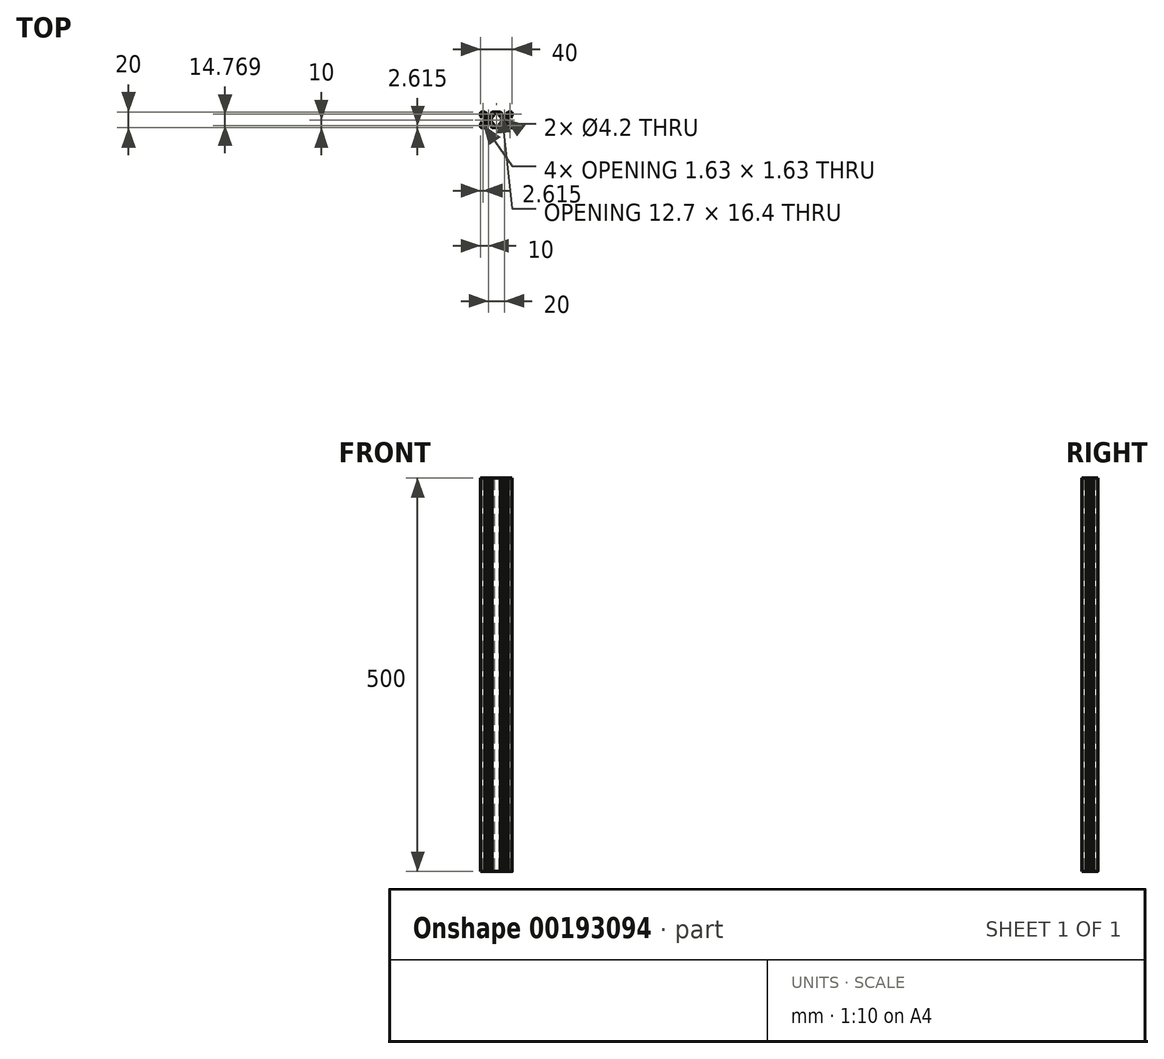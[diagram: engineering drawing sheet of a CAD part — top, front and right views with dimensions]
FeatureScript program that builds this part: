
annotation { "Feature Type Name" : "Feature", "Feature Type Description" : "" }
export const myFeature = defineFeature(function(context is Context, id is Id, definition is map)
    precondition{}
    {
        {
            var Q0;
            Q0=qCreatedBy(makeId("Top.planeOp"),FACE);
            var sketch = newSketch(context, id + "F0", { "sketchPlane" : qUnion([Q0])});
            skLineSegment(sketch, "E0", {"start": v(8.5, -10) * mm, "end": v(4.64, -10) * mm});
            skLineSegment(sketch, "E1", {"start": v(-10, -8.5) * mm, "end": v(-10, -4.64) * mm});
            skLineSegment(sketch, "E2", {"start": v(-8.5, 10) * mm, "end": v(-4.64, 10) * mm});
            skLineSegment(sketch, "E3.0", {"start": v(-5.5, 8.2) * mm, "end": v(-2.84, 8.2) * mm});
            skLineSegment(sketch, "E3.1", {"start": v(-8.2, -5.5) * mm, "end": v(-8.2, -2.84) * mm});
            skLineSegment(sketch, "E3.2", {"start": v(5.5, -8.2) * mm, "end": v(2.84, -8.2) * mm});
            skLineSegment(sketch, "E4.trimOffspring", {"start": v(4.64, 10) * mm, "end": v(8.5, 10) * mm});
            skLineSegment(sketch, "E5", {"start": v(-2.84, 8.2) * mm, "end": v(-4.64, 10) * mm});
            skLineSegment(sketch, "E6.trimOffspring", {"start": v(2.84, 8.2) * mm, "end": v(5.5, 8.2) * mm});
            skLineSegment(sketch, "E7.MirrorCS", {"start": v(2.84, 8.2) * mm, "end": v(4.64, 10) * mm});
            skLineSegment(sketch, "E8.MirrorCS", {"start": v(2.84, -8.2) * mm, "end": v(4.64, -10) * mm});
            skLineSegment(sketch, "E9.MirrorCS", {"start": v(-2.84, -8.2) * mm, "end": v(-4.64, -10) * mm});
            skLineSegment(sketch, "E10.trimOffspring", {"start": v(-2.84, -8.2) * mm, "end": v(-5.5, -8.2) * mm});
            skLineSegment(sketch, "E11.trimOffspring", {"start": v(-4.64, -10) * mm, "end": v(-8.5, -10) * mm});
            skLineSegment(sketch, "E12", {"start": v(-8.2, 2.84) * mm, "end": v(-10, 4.64) * mm});
            skLineSegment(sketch, "E13", {"start": v(-8.2, -2.84) * mm, "end": v(-10, -4.64) * mm});
            skLineSegment(sketch, "E14.trimOffspring", {"start": v(-10, 4.64) * mm, "end": v(-10, 8.5) * mm});
            skLineSegment(sketch, "E15.trimOffspring", {"start": v(-8.2, 2.84) * mm, "end": v(-8.2, 5.5) * mm});
            skCircle(sketch, "E16", {"center": v(0, 0) * mm, "radius": 2.1 * mm});
            skLineSegment(sketch, "E17", {"start": v(-6.56, 5.5) * mm, "end": v(-3.9, 2.84) * mm});
            skLineSegment(sketch, "E18", {"start": v(-5.5, 6.56) * mm, "end": v(-2.84, 3.9) * mm});
            skLineSegment(sketch, "E19", {"start": v(-5.5, 6.56) * mm, "end": v(-5.5, 8.2) * mm});
            skLineSegment(sketch, "E20", {"start": v(-6.56, 5.5) * mm, "end": v(-8.2, 5.5) * mm});
            skLineSegment(sketch, "E21", {"start": v(6.56, 5.5) * mm, "end": v(3.9, 2.84) * mm});
            skLineSegment(sketch, "E22", {"start": v(5.5, 6.56) * mm, "end": v(2.84, 3.9) * mm});
            skLineSegment(sketch, "E23", {"start": v(-6.56, -5.5) * mm, "end": v(-8.2, -5.5) * mm});
            skLineSegment(sketch, "E24", {"start": v(-5.5, -6.56) * mm, "end": v(-5.5, -8.2) * mm});
            skLineSegment(sketch, "E25", {"start": v(5.5, 6.56) * mm, "end": v(5.5, 8.2) * mm});
            skLineSegment(sketch, "E26", {"start": v(5.5, -6.56) * mm, "end": v(5.5, -8.2) * mm});
            skLineSegment(sketch, "E27.trimOffspring", {"start": v(2.84, -3.9) * mm, "end": v(5.5, -6.56) * mm});
            skLineSegment(sketch, "E28.trimOffspring", {"start": v(-2.84, -3.9) * mm, "end": v(-5.5, -6.56) * mm});
            skLineSegment(sketch, "E29.trimOffspring", {"start": v(-3.9, -2.84) * mm, "end": v(-6.56, -5.5) * mm});
            skLineSegment(sketch, "E30.trimOffspring", {"start": v(3.9, -2.84) * mm, "end": v(6.56, -5.5) * mm});
            skLineSegment(sketch, "E31", {"start": v(-3.9, -2.84) * mm, "end": v(-3.9, -0.25) * mm});
            skLineSegment(sketch, "E32", {"start": v(-2.84, 3.9) * mm, "end": v(-0.25, 3.9) * mm});
            skLineSegment(sketch, "E33", {"start": v(-2.84, -3.9) * mm, "end": v(-0.25, -3.9) * mm});
            skLineSegment(sketch, "E34", {"start": v(3.9, 2.84) * mm, "end": v(3.9, 0.25) * mm});
            skLineSegment(sketch, "E35", {"start": v(-8.2, 6.57) * mm, "end": v(-8.2, 8.2) * mm});
            skLineSegment(sketch, "E36", {"start": v(-6.57, 8.2) * mm, "end": v(-8.2, 8.2) * mm});
            skLineSegment(sketch, "E37", {"start": v(-8.2, 6.57) * mm, "end": v(-7.63, 6.57) * mm});
            skLineSegment(sketch, "E38", {"start": v(-6.57, 8.2) * mm, "end": v(-6.57, 7.63) * mm});
            skLineSegment(sketch, "E39", {"start": v(-7.63, 6.57) * mm, "end": v(-6.57, 7.63) * mm});
            skLineSegment(sketch, "E40.MirrorCS", {"start": v(-6.57, -8.2) * mm, "end": v(-8.2, -8.2) * mm});
            skLineSegment(sketch, "E41.MirrorCS", {"start": v(-8.2, -6.57) * mm, "end": v(-7.63, -6.57) * mm});
            skLineSegment(sketch, "E42.MirrorCS", {"start": v(-8.2, -6.57) * mm, "end": v(-8.2, -8.2) * mm});
            skLineSegment(sketch, "E43.MirrorCS", {"start": v(-7.63, -6.57) * mm, "end": v(-6.57, -7.63) * mm});
            skLineSegment(sketch, "E44.MirrorCS", {"start": v(-6.57, -8.2) * mm, "end": v(-6.57, -7.63) * mm});
            skArc(sketch, "E45.filletArc", {"start": v(-8.5, 10) * mm, "mid": v(-9.56, 9.56) * mm, "end": v(-10, 8.5) * mm});
            skPoint(sketch, "E46.visualSharp", {"position": v(10, 10) * mm});
            skArc(sketch, "E47.filletArc", {"start": v(-10, -8.5) * mm, "mid": v(-9.56, -9.56) * mm, "end": v(-8.5, -10) * mm});
            skLineSegment(sketch, "E48", {"start": v(-3.65, 0) * mm, "end": v(-3.9, 0.25) * mm});
            skLineSegment(sketch, "E49.MirrorCS", {"start": v(-3.65, 0) * mm, "end": v(-3.9, -0.25) * mm});
            skLineSegment(sketch, "E50.trimOffspring", {"start": v(-3.9, 0.25) * mm, "end": v(-3.9, 2.84) * mm});
            skLineSegment(sketch, "E51.MirrorCS", {"start": v(3.65, 0) * mm, "end": v(3.9, 0.25) * mm});
            skLineSegment(sketch, "E52.MirrorCS", {"start": v(3.65, 0) * mm, "end": v(3.9, -0.25) * mm});
            skLineSegment(sketch, "E53", {"start": v(0, -3.65) * mm, "end": v(0.25, -3.9) * mm});
            skLineSegment(sketch, "E54.MirrorCS", {"start": v(0, -3.65) * mm, "end": v(-0.25, -3.9) * mm});
            skLineSegment(sketch, "E55.trimOffspring", {"start": v(0.25, -3.9) * mm, "end": v(2.84, -3.9) * mm});
            skLineSegment(sketch, "E56.trimOffspring", {"start": v(3.9, -0.25) * mm, "end": v(3.9, -2.84) * mm});
            skLineSegment(sketch, "E57.MirrorCS", {"start": v(0, 3.65) * mm, "end": v(-0.25, 3.9) * mm});
            skLineSegment(sketch, "E58.MirrorCS", {"start": v(0, 3.65) * mm, "end": v(0.25, 3.9) * mm});
            skLineSegment(sketch, "E59.trimOffspring", {"start": v(0.25, 3.9) * mm, "end": v(2.84, 3.9) * mm});
            skLineSegment(sketch, "E60.MirrorCS", {"start": v(20, -3.65) * mm, "end": v(19.75, -3.9) * mm});
            skLineSegment(sketch, "E61.MirrorCS", {"start": v(20, -3.65) * mm, "end": v(20.25, -3.9) * mm});
            skLineSegment(sketch, "E62.MirrorCS", {"start": v(23.65, 0) * mm, "end": v(23.9, 0.25) * mm});
            skLineSegment(sketch, "E63.MirrorCS", {"start": v(23.65, 0) * mm, "end": v(23.9, -0.25) * mm});
            skLineSegment(sketch, "E64.MirrorCS", {"start": v(16.35, 0) * mm, "end": v(16.1, 0.25) * mm});
            skLineSegment(sketch, "E65.MirrorCS", {"start": v(16.35, 0) * mm, "end": v(16.1, -0.25) * mm});
            skLineSegment(sketch, "E66.MirrorCS", {"start": v(28.2, -6.57) * mm, "end": v(27.63, -6.57) * mm});
            skLineSegment(sketch, "E67.MirrorCS", {"start": v(20, 3.65) * mm, "end": v(20.25, 3.9) * mm});
            skLineSegment(sketch, "E68.MirrorCS", {"start": v(20, 3.65) * mm, "end": v(19.75, 3.9) * mm});
            skLineSegment(sketch, "E69.MirrorCS", {"start": v(28.2, 6.57) * mm, "end": v(27.63, 6.57) * mm});
            skLineSegment(sketch, "E70.MirrorCS", {"start": v(26.57, -8.2) * mm, "end": v(26.57, -7.63) * mm});
            skLineSegment(sketch, "E71.MirrorCS", {"start": v(26.57, 8.2) * mm, "end": v(26.57, 7.63) * mm});
            skLineSegment(sketch, "E72.MirrorCS", {"start": v(28.2, 2.84) * mm, "end": v(28.2, 5.5) * mm});
            skLineSegment(sketch, "E73.MirrorCS", {"start": v(14.5, -6.56) * mm, "end": v(14.5, -8.2) * mm});
            skArc(sketch, "E74.MirrorCS", {"start": v(30, -8.5) * mm, "mid": v(29.56, -9.56) * mm, "end": v(28.5, -10) * mm});
            skLineSegment(sketch, "E75.MirrorCS", {"start": v(17.16, -3.9) * mm, "end": v(14.5, -6.56) * mm});
            skLineSegment(sketch, "E76.MirrorCS", {"start": v(22.84, -3.9) * mm, "end": v(25.5, -6.56) * mm});
            skPoint(sketch, "E77.MirrorP", {"position": v(10, -10) * mm});
            skLineSegment(sketch, "E78.MirrorCS", {"start": v(23.9, -2.84) * mm, "end": v(26.56, -5.5) * mm});
            skLineSegment(sketch, "E79.MirrorCS", {"start": v(23.9, 0.25) * mm, "end": v(23.9, 2.84) * mm});
            skLineSegment(sketch, "E80.MirrorCS", {"start": v(16.1, -2.84) * mm, "end": v(13.44, -5.5) * mm});
            skCircle(sketch, "E81.MirrorC", {"center": v(20, 0) * mm, "radius": 2.1 * mm});
            skLineSegment(sketch, "E82.MirrorCS", {"start": v(23.9, -2.84) * mm, "end": v(23.9, -0.25) * mm});
            skLineSegment(sketch, "E83.MirrorCS", {"start": v(26.56, 5.5) * mm, "end": v(23.9, 2.84) * mm});
            skLineSegment(sketch, "E84.MirrorCS", {"start": v(22.84, 3.9) * mm, "end": v(20.25, 3.9) * mm});
            skLineSegment(sketch, "E85.MirrorCS", {"start": v(25.5, 6.56) * mm, "end": v(22.84, 3.9) * mm});
            skLineSegment(sketch, "E86.MirrorCS", {"start": v(22.84, -3.9) * mm, "end": v(20.25, -3.9) * mm});
            skLineSegment(sketch, "E87.MirrorCS", {"start": v(25.5, 6.56) * mm, "end": v(25.5, 8.2) * mm});
            skLineSegment(sketch, "E88.MirrorCS", {"start": v(16.1, -0.25) * mm, "end": v(16.1, -2.84) * mm});
            skLineSegment(sketch, "E89.MirrorCS", {"start": v(28.2, 6.57) * mm, "end": v(28.2, 8.2) * mm});
            skLineSegment(sketch, "E90.MirrorCS", {"start": v(13.44, 5.5) * mm, "end": v(16.1, 2.84) * mm});
            skLineSegment(sketch, "E91.MirrorCS", {"start": v(26.57, -8.2) * mm, "end": v(28.2, -8.2) * mm});
            skLineSegment(sketch, "E92.MirrorCS", {"start": v(16.1, 2.84) * mm, "end": v(16.1, 0.25) * mm});
            skLineSegment(sketch, "E93.MirrorCS", {"start": v(26.56, 5.5) * mm, "end": v(28.2, 5.5) * mm});
            skLineSegment(sketch, "E94.MirrorCS", {"start": v(19.75, -3.9) * mm, "end": v(17.16, -3.9) * mm});
            skLineSegment(sketch, "E95.MirrorCS", {"start": v(28.2, -6.57) * mm, "end": v(28.2, -8.2) * mm});
            skLineSegment(sketch, "E96.MirrorCS", {"start": v(26.57, 8.2) * mm, "end": v(28.2, 8.2) * mm});
            skLineSegment(sketch, "E97.MirrorCS", {"start": v(14.5, 6.56) * mm, "end": v(17.16, 3.9) * mm});
            skLineSegment(sketch, "E98.MirrorCS", {"start": v(27.63, -6.57) * mm, "end": v(26.57, -7.63) * mm});
            skLineSegment(sketch, "E99.MirrorCS", {"start": v(26.56, -5.5) * mm, "end": v(28.2, -5.5) * mm});
            skLineSegment(sketch, "E100.MirrorCS", {"start": v(22.84, -8.2) * mm, "end": v(24.64, -10) * mm});
            skLineSegment(sketch, "E101.MirrorCS", {"start": v(22.84, -8.2) * mm, "end": v(25.5, -8.2) * mm});
            skLineSegment(sketch, "E102.MirrorCS", {"start": v(24.64, -10) * mm, "end": v(28.5, -10) * mm});
            skLineSegment(sketch, "E103.MirrorCS", {"start": v(11.5, -10) * mm, "end": v(15.36, -10) * mm});
            skLineSegment(sketch, "E104.MirrorCS", {"start": v(30, -8.5) * mm, "end": v(30, -4.64) * mm});
            skLineSegment(sketch, "E105.MirrorCS", {"start": v(28.5, 10) * mm, "end": v(24.64, 10) * mm});
            skLineSegment(sketch, "E106.MirrorCS", {"start": v(25.5, 8.2) * mm, "end": v(22.84, 8.2) * mm});
            skLineSegment(sketch, "E107.MirrorCS", {"start": v(28.2, -5.5) * mm, "end": v(28.2, -2.84) * mm});
            skLineSegment(sketch, "E108.MirrorCS", {"start": v(14.5, -8.2) * mm, "end": v(17.16, -8.2) * mm});
            skLineSegment(sketch, "E109.MirrorCS", {"start": v(15.36, 10) * mm, "end": v(11.5, 10) * mm});
            skLineSegment(sketch, "E110.MirrorCS", {"start": v(22.84, 8.2) * mm, "end": v(24.64, 10) * mm});
            skLineSegment(sketch, "E111.MirrorCS", {"start": v(17.16, 8.2) * mm, "end": v(14.5, 8.2) * mm});
            skLineSegment(sketch, "E112.MirrorCS", {"start": v(17.16, 8.2) * mm, "end": v(15.36, 10) * mm});
            skLineSegment(sketch, "E113.MirrorCS", {"start": v(17.16, -8.2) * mm, "end": v(15.36, -10) * mm});
            skLineSegment(sketch, "E114.MirrorCS", {"start": v(28.2, 2.84) * mm, "end": v(30, 4.64) * mm});
            skLineSegment(sketch, "E115.MirrorCS", {"start": v(19.75, 3.9) * mm, "end": v(17.16, 3.9) * mm});
            skLineSegment(sketch, "E116.MirrorCS", {"start": v(25.5, -6.56) * mm, "end": v(25.5, -8.2) * mm});
            skLineSegment(sketch, "E117.MirrorCS", {"start": v(28.2, -2.84) * mm, "end": v(30, -4.64) * mm});
            skArc(sketch, "E118.MirrorCS", {"start": v(28.5, 10) * mm, "mid": v(29.56, 9.56) * mm, "end": v(30, 8.5) * mm});
            skLineSegment(sketch, "E119.MirrorCS", {"start": v(27.63, 6.57) * mm, "end": v(26.57, 7.63) * mm});
            skLineSegment(sketch, "E120.MirrorCS", {"start": v(14.5, 6.56) * mm, "end": v(14.5, 8.2) * mm});
            skLineSegment(sketch, "E121.MirrorCS", {"start": v(30, 4.64) * mm, "end": v(30, 8.5) * mm});
            skLineSegment(sketch, "E122", {"start": v(8.5, 10) * mm, "end": v(11.5, 10) * mm});
            skLineSegment(sketch, "E123", {"start": v(8.5, -10) * mm, "end": v(11.5, -10) * mm});
            skLineSegment(sketch, "E124", {"start": v(7, 8.2) * mm, "end": v(13, 8.2) * mm});
            skLineSegment(sketch, "E125", {"start": v(7, -8.2) * mm, "end": v(7, -5.94) * mm});
            skLineSegment(sketch, "E126", {"start": v(3.9, -2.84) * mm, "end": v(7, -5.94) * mm});
            skLineSegment(sketch, "E127", {"start": v(13, -8.2) * mm, "end": v(13, -5.94) * mm});
            skLineSegment(sketch, "E128", {"start": v(16.1, -2.84) * mm, "end": v(13, -5.94) * mm});
            skLineSegment(sketch, "E129", {"start": v(7, -8.2) * mm, "end": v(13, -8.2) * mm});
            skLineSegment(sketch, "E130", {"start": v(16.1, 2.84) * mm, "end": v(13, 5.94) * mm});
            skLineSegment(sketch, "E131", {"start": v(3.9, 2.84) * mm, "end": v(6.56, 5.5) * mm});
            skLineSegment(sketch, "E132", {"start": v(6.56, 5.5) * mm, "end": v(7, 5.94) * mm});
            skLineSegment(sketch, "E133.trimOffspring", {"start": v(7, 5.94) * mm, "end": v(7, 8.2) * mm});
            skLineSegment(sketch, "E134", {"start": v(13, 5.94) * mm, "end": v(13, 8.2) * mm});
            skSolve(sketch);
        }
        {
            var Q0;
            Q0=makeQuery(id+"F0.imprint","IMPRINT",FACE,{"disambiguationData":[TD([[makeQuery(id+"F0.imprint","IMPRINT",EDGE,{"derivedFrom":sQuery(id+"F0.wireOp",EDGE,"E0")}),-1.0]])]});
            extrude(context, id + "F1", {"entities" : qUnion([Q0]), "depth" : 500 * mm});
        }
    });
